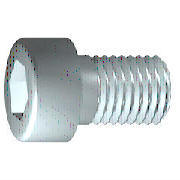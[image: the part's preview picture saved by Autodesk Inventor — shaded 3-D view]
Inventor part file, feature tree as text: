
AUTODESK INVENTOR PART (.ipt)
format: ipt  version: 2023.3 (Build 273359000, 359)  size: 193,536 bytes
history: native  units: mm (DEFAULTED — no unit token found)
features: sketch x2, other x1, extrude x1, plane x1, fillet x1
ambient origin geometry x7: Origin, YZ Plane, XY Plane, X Axis, Y Axis, Z Axis, Center Point
bodies: Solid1 (feature_tree)
feature tree (6):
  other  "Körper"
  extrude  "Loch"  Depth=3.0mm
  plane  "Work Plane1"
  fillet  "Fillet2"  Radius=3.0mm
  sketch  "Skizze1"  dims[d1=4.75mm d2=0.306825mm d3=3.0mm]
  sketch  "Skizze2"  dims[d4=1.3mm d5=60.0deg d6=3.0mm d7=3.0mm d8=2.886751mm d9=5.5mm d10=90.0deg d11=10.0mm d12=0.0mm d13=4.75mm d14=0.0mm d15=0.306725mm d16=0.306725mm d17=0.3mm d19=0.0mm d26=6.0mm d27=45.0deg d28=0.0mm d29=0.0mm d30=0.1mm]
